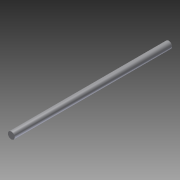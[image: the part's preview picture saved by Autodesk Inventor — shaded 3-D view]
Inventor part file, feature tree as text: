
AUTODESK INVENTOR PART (.ipt)
format: ipt  version: 2012 SP2 (Build 160219200, 219)  size: 65,024 bytes
history: native  units: in
note: dims shown in document units (in); Inventor stores cm internally (conversion verified against a paired STEP export)
features: extrude x1, sketch x1, reference x1
ambient origin geometry x8: Origin, YZ Plane, XZ Plane, XY Plane, X Axis, Y Axis, Z Axis, Center Point
bodies: Solid1 (feature_tree)
feature tree (3):
  extrude  "Extrusion1"  [1 undecoded]
  sketch  "Sketch1"  dims[d0=0.3937in d1=17.7594in d2=0.0in d3=0.0in]
  reference  "Reference1"
note: 1 required parameter value undecoded (feature->parameter linkage not recoverable at this tier; creation-order binding heuristic only, values carry confidence <= 0.55)
